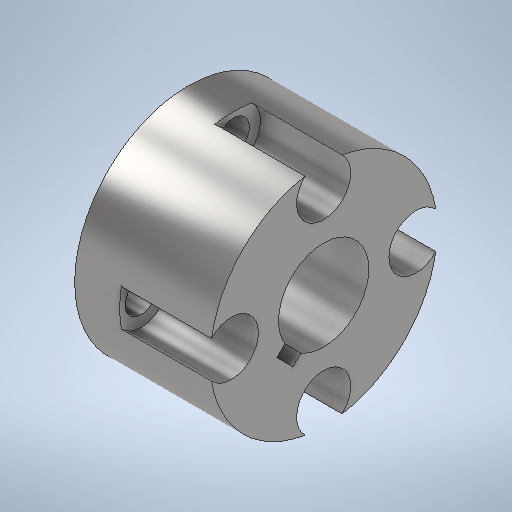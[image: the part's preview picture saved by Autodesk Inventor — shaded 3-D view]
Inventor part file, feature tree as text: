
AUTODESK INVENTOR PART (.ipt)
format: ipt  version: 2025.1 (Build 291241020, 241B)  size: 383,488 bytes
history: native  units: in
note: dims shown in document units (in); Inventor stores cm internally (conversion verified against a paired STEP export)
features: sketch x11, extrude x6, hole x4, projected_geometry x3, plane x1
ambient origin geometry x8: Origin, YZ Plane, XZ Plane, XY Plane, X Axis, Y Axis, Z Axis, Center Point
bodies: Solid1 (feature_tree)
feature tree (25):
  extrude  "Extrusion1"  Depth=0.1575in
  extrude  "Extrusion2"  Depth=0.5118in
  plane  "Work Plane1"
  extrude  "Extrusion4"  Depth=0.5in
  extrude  "Extrusion5"  Depth=0.5906in
  extrude  "Extrusion6"  Depth=0.3937in
  extrude  "Extrusion7"  Depth=0.3in
  hole  "Hole1"  [1 undecoded]
  hole  "Hole2"  [1 undecoded]
  hole  "Hole3"  [1 undecoded]
  hole  "Hole4"  [1 undecoded]
  sketch  "Sketch1"  dims[d0=1.2598in d1=0.1575in]
  sketch  "Sketch Circular Pattern1"  dims[d2=1.0236in d3=0.5118in]
  sketch  "Sketch2"  dims[d4=1.5748in d6=360.0deg d8=0.5in]
  projected_geometry  "Projected Loop1"
  sketch  "Sketch6"  dims[d9=0.1181in d10=0.0in d11=0.5906in]
  projected_geometry  "Projected Loop3"
  sketch  "Sketch7"  dims[d12=0.3937in d13=0.0in d18=0.595in]
  sketch  "Sketch8"  dims[d19=1.0in d20=0.0in d21=0.3in]
  sketch  "Sketch9"  dims[d22=0.3in d23=0.3in]
  projected_geometry  "Projected Loop4"
  sketch  "Sketch10"  dims[d24=0.3in d25=1.0in d26=0.0in]
  sketch  "Sketch11"  dims[d27=0.0625in d28=0.0625in]
  sketch  "Sketch12"  dims[d29=0.0625in d30=0.0625in]
  sketch  "Sketch13"  dims[d31=90.0deg d32=0.0in d33=90.0deg d34=0.125in d35=90.0deg d36=0.5625in d37=0.0in d38=0.238in d39=0.0in d40=0.177in d41=0.75in d42=0.3in d43=0.5in d44=0.5635in d45=1.0in d46=0.8108in d47=0.177in d48=0.75in d49=0.3in d50=0.5in d51=0.5635in d52=1.0in d53=0.8108in d54=0.177in d55=0.75in d56=0.3in d57=0.5in d58=0.5635in d59=1.0in d60=0.8108in d61=0.177in d62=0.75in d63=0.3in d64=0.5in d65=0.5635in d66=1.0in d67=0.8108in]
note: 4 required parameter values undecoded (feature->parameter linkage not recoverable at this tier; creation-order binding heuristic only, values carry confidence <= 0.55)
